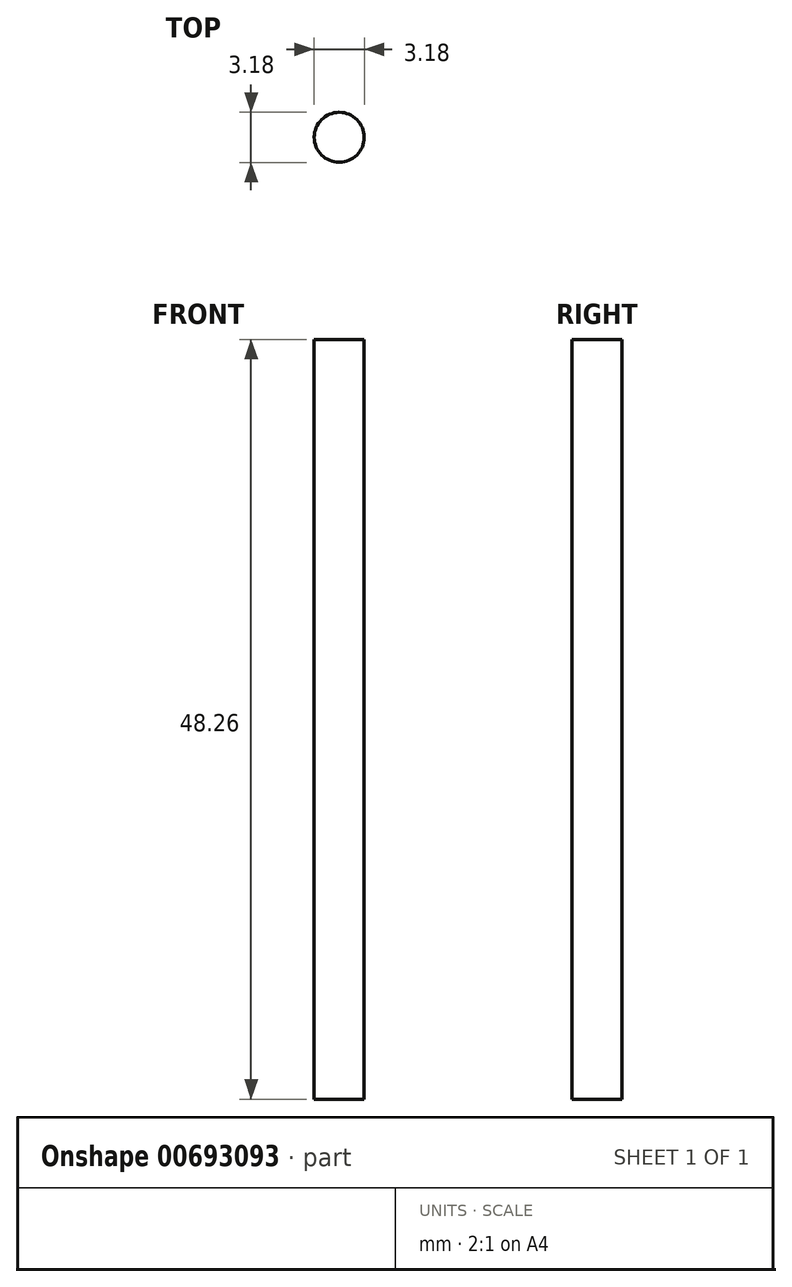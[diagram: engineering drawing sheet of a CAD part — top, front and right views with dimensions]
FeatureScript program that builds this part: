
annotation { "Feature Type Name" : "Feature", "Feature Type Description" : "" }
export const myFeature = defineFeature(function(context is Context, id is Id, definition is map)
    precondition{}
    {
        {
            var Q0;
            Q0=qCreatedBy(makeId("Top.planeOp"),FACE);
            var sketch = newSketch(context, id + "F0", { "sketchPlane" : qUnion([Q0])});
            skCircle(sketch, "E0", {"center": v(0, 0) * mm, "radius": 1.59 * mm});
            skSolve(sketch);
        }
        {
            var Q0;
            Q0=makeQuery(id+"F0.imprint","IMPRINT",FACE,{"disambiguationData":[TD([[makeQuery(id+"F0.imprint","IMPRINT",EDGE,{"derivedFrom":sQuery(id+"F0.wireOp",EDGE,"E0")}),1.0]])]});
            extrude(context, id + "F1", {"entities" : qUnion([Q0]), "depth" : 48.26 * mm, "offsetDistance" : 25.4 * mm});
        }
    });
